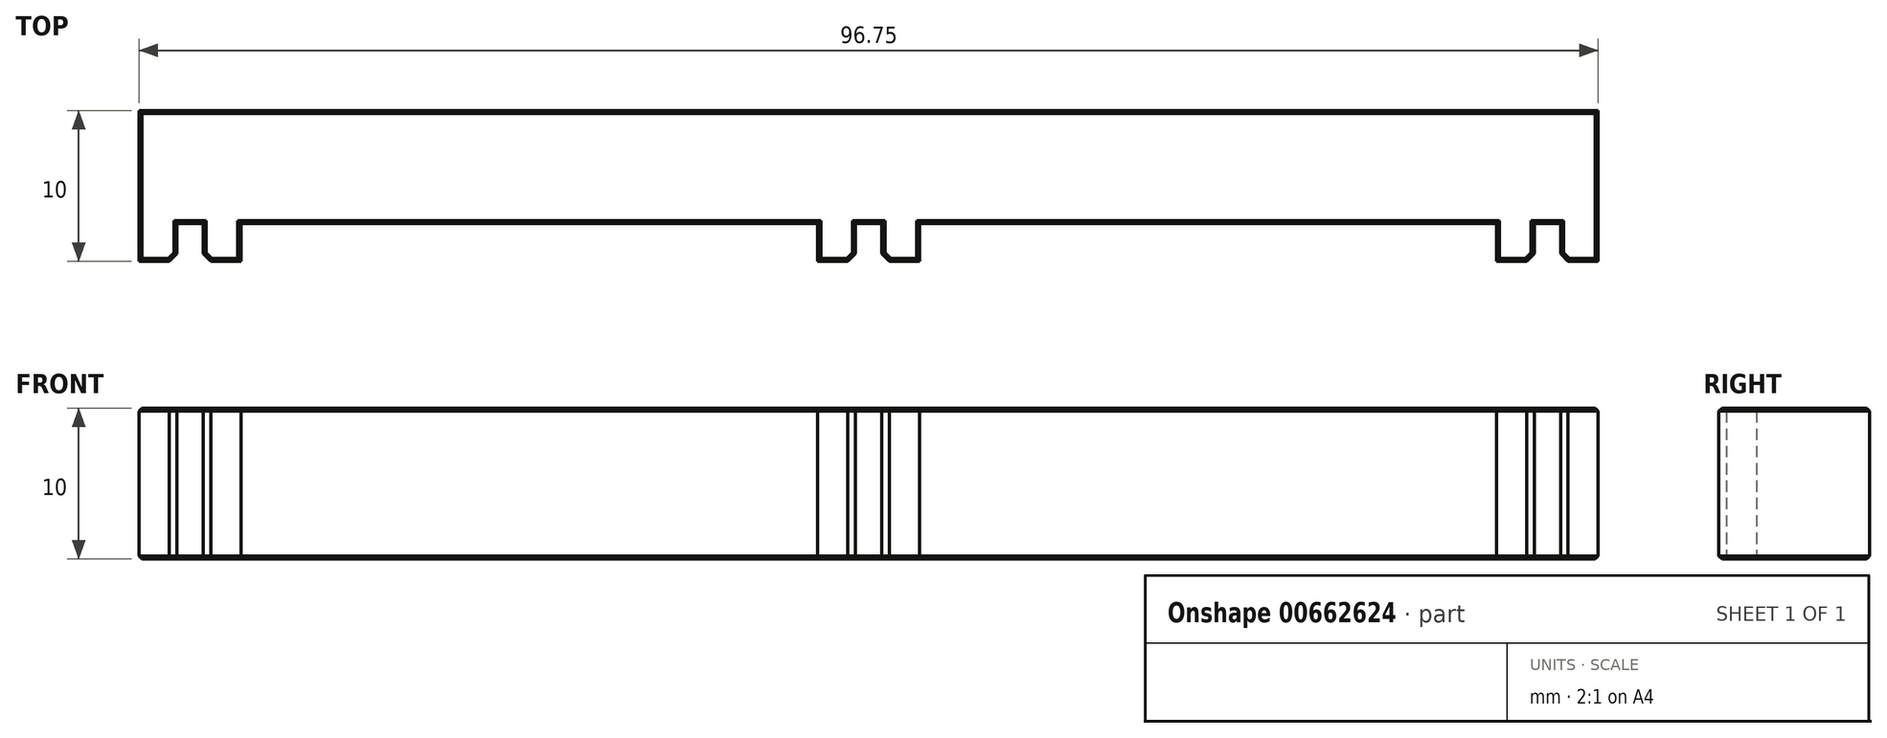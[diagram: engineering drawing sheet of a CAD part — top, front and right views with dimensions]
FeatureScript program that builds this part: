
annotation { "Feature Type Name" : "Feature", "Feature Type Description" : "" }
export const myFeature = defineFeature(function(context is Context, id is Id, definition is map)
    precondition{}
    {
        {
            var Q0;
            Q0=qCreatedBy(makeId("Top.planeOp"),FACE);
            var sketch = newSketch(context, id + "F0", { "sketchPlane" : qUnion([Q0])});
            skLineSegment(sketch, "E0", {"start": v(-51.46, 0) * mm, "end": v(-51.46, 10) * mm});
            skLineSegment(sketch, "E1", {"start": v(-51.46, 10) * mm, "end": v(45.3, 10) * mm});
            skLineSegment(sketch, "E2", {"start": v(45.3, 10) * mm, "end": v(45.3, 0) * mm});
            skLineSegment(sketch, "E3", {"start": v(45.3, 0) * mm, "end": v(42.8, 0) * mm});
            skLineSegment(sketch, "E4", {"start": v(42.8, 0) * mm, "end": v(42.8, 2.5) * mm});
            skLineSegment(sketch, "E5", {"start": v(42.8, 2.5) * mm, "end": v(41.04, 2.5) * mm});
            skLineSegment(sketch, "E6", {"start": v(41.04, 2.5) * mm, "end": v(41.04, 0) * mm});
            skLineSegment(sketch, "E7", {"start": v(41.04, 0) * mm, "end": v(38.54, 0) * mm});
            skLineSegment(sketch, "E8", {"start": v(38.54, 2.5) * mm, "end": v(38.54, 0) * mm});
            skLineSegment(sketch, "E9", {"start": v(38.54, 2.5) * mm, "end": v(0.3, 2.5) * mm});
            skLineSegment(sketch, "E10", {"start": v(0.3, 2.5) * mm, "end": v(0.3, 0) * mm});
            skLineSegment(sketch, "E11", {"start": v(0.3, 0) * mm, "end": v(-2.2, 0) * mm});
            skLineSegment(sketch, "E12", {"start": v(-2.2, 2.5) * mm, "end": v(-2.2, 0) * mm});
            skLineSegment(sketch, "E13", {"start": v(-2.2, 2.5) * mm, "end": v(-3.96, 2.5) * mm});
            skLineSegment(sketch, "E14", {"start": v(-3.96, 2.5) * mm, "end": v(-3.96, 0) * mm});
            skLineSegment(sketch, "E15", {"start": v(-3.96, 0) * mm, "end": v(-6.46, 0) * mm});
            skLineSegment(sketch, "E16", {"start": v(-6.46, 2.5) * mm, "end": v(-6.46, 0) * mm});
            skLineSegment(sketch, "E17", {"start": v(-6.46, 2.5) * mm, "end": v(-44.7, 2.5) * mm});
            skLineSegment(sketch, "E18", {"start": v(-44.7, 2.5) * mm, "end": v(-44.7, 0) * mm});
            skLineSegment(sketch, "E19", {"start": v(-44.7, 0) * mm, "end": v(-47.2, 0) * mm});
            skLineSegment(sketch, "E20", {"start": v(-47.2, 0) * mm, "end": v(-47.2, 2.5) * mm});
            skLineSegment(sketch, "E21", {"start": v(-47.2, 2.5) * mm, "end": v(-48.96, 2.5) * mm});
            skLineSegment(sketch, "E22", {"start": v(-48.96, 2.5) * mm, "end": v(-48.96, 0) * mm});
            skLineSegment(sketch, "E23", {"start": v(-48.96, 0) * mm, "end": v(-51.46, 0) * mm});
            skSolve(sketch);
        }
        {
            var Q0;
            Q0=makeQuery(id+"F0.imprint","IMPRINT",FACE,{"disambiguationData":[TD([[makeQuery(id+"F0.imprint","IMPRINT",EDGE,{"derivedFrom":sQuery(id+"F0.wireOp",EDGE,"E0")}),-1.0]])]});
            extrude(context, id + "F1", {"entities" : qUnion([Q0]), "depth" : 10 * mm, "offsetDistance" : 25 * mm});
        }
        {
            var Q0;
            Q0=makeQuery(id+"F1.opExtrude","SWEPT_EDGE",EDGE,{"disambiguationData":[OSD([sQuery(id+"F0.wireOp",EDGE,"E22"),sQuery(id+"F0.wireOp",EDGE,"E23")])]});
            var Q1;
            Q1=makeQuery(id+"F1.opExtrude","SWEPT_EDGE",EDGE,{"disambiguationData":[OSD([sQuery(id+"F0.wireOp",EDGE,"E19"),sQuery(id+"F0.wireOp",EDGE,"E20")])]});
            var Q2;
            Q2=makeQuery(id+"F1.opExtrude","SWEPT_EDGE",EDGE,{"disambiguationData":[OSD([sQuery(id+"F0.wireOp",EDGE,"E11"),sQuery(id+"F0.wireOp",EDGE,"E12")])]});
            var Q3;
            Q3=makeQuery(id+"F1.opExtrude","SWEPT_EDGE",EDGE,{"disambiguationData":[OSD([sQuery(id+"F0.wireOp",EDGE,"E14"),sQuery(id+"F0.wireOp",EDGE,"E15")])]});
            var Q4;
            Q4=makeQuery(id+"F1.opExtrude","SWEPT_EDGE",EDGE,{"disambiguationData":[OSD([sQuery(id+"F0.wireOp",EDGE,"E3"),sQuery(id+"F0.wireOp",EDGE,"E4")])]});
            var Q5;
            Q5=makeQuery(id+"F1.opExtrude","SWEPT_EDGE",EDGE,{"disambiguationData":[OSD([sQuery(id+"F0.wireOp",EDGE,"E6"),sQuery(id+"F0.wireOp",EDGE,"E7")])]});
            chamfer(context, id + "F2", {"entities" : qUnion([Q0, Q1, Q2, Q3, Q4, Q5]), "width" : .5 * mm, "tangentPropagation" : true});
        }
        {
            var Q0;
            Q0=makeQuery(id+"F1.opExtrude","CAP_FACE",FACE,{"disambiguationData":[OSD([sQuery(id+"F0.wireOp",EDGE,"E0"),sQuery(id+"F0.wireOp",EDGE,"E1"),sQuery(id+"F0.wireOp",EDGE,"E2"),sQuery(id+"F0.wireOp",EDGE,"E3"),sQuery(id+"F0.wireOp",EDGE,"E4"),sQuery(id+"F0.wireOp",EDGE,"E5"),sQuery(id+"F0.wireOp",EDGE,"E6"),sQuery(id+"F0.wireOp",EDGE,"E7"),sQuery(id+"F0.wireOp",EDGE,"E8"),sQuery(id+"F0.wireOp",EDGE,"E9"),sQuery(id+"F0.wireOp",EDGE,"E10"),sQuery(id+"F0.wireOp",EDGE,"E11"),sQuery(id+"F0.wireOp",EDGE,"E12"),sQuery(id+"F0.wireOp",EDGE,"E13"),sQuery(id+"F0.wireOp",EDGE,"E14"),sQuery(id+"F0.wireOp",EDGE,"E15"),sQuery(id+"F0.wireOp",EDGE,"E16"),sQuery(id+"F0.wireOp",EDGE,"E17"),sQuery(id+"F0.wireOp",EDGE,"E18"),sQuery(id+"F0.wireOp",EDGE,"E19"),sQuery(id+"F0.wireOp",EDGE,"E20"),sQuery(id+"F0.wireOp",EDGE,"E21"),sQuery(id+"F0.wireOp",EDGE,"E22"),sQuery(id+"F0.wireOp",EDGE,"E23")])],"isStart":false});
            var Q1;
            Q1=makeQuery(id+"F1.opExtrude","CAP_FACE",FACE,{"disambiguationData":[OSD([sQuery(id+"F0.wireOp",EDGE,"E0"),sQuery(id+"F0.wireOp",EDGE,"E1"),sQuery(id+"F0.wireOp",EDGE,"E2"),sQuery(id+"F0.wireOp",EDGE,"E3"),sQuery(id+"F0.wireOp",EDGE,"E4"),sQuery(id+"F0.wireOp",EDGE,"E5"),sQuery(id+"F0.wireOp",EDGE,"E6"),sQuery(id+"F0.wireOp",EDGE,"E7"),sQuery(id+"F0.wireOp",EDGE,"E8"),sQuery(id+"F0.wireOp",EDGE,"E9"),sQuery(id+"F0.wireOp",EDGE,"E10"),sQuery(id+"F0.wireOp",EDGE,"E11"),sQuery(id+"F0.wireOp",EDGE,"E12"),sQuery(id+"F0.wireOp",EDGE,"E13"),sQuery(id+"F0.wireOp",EDGE,"E14"),sQuery(id+"F0.wireOp",EDGE,"E15"),sQuery(id+"F0.wireOp",EDGE,"E16"),sQuery(id+"F0.wireOp",EDGE,"E17"),sQuery(id+"F0.wireOp",EDGE,"E18"),sQuery(id+"F0.wireOp",EDGE,"E19"),sQuery(id+"F0.wireOp",EDGE,"E20"),sQuery(id+"F0.wireOp",EDGE,"E21"),sQuery(id+"F0.wireOp",EDGE,"E22"),sQuery(id+"F0.wireOp",EDGE,"E23")])],"isStart":true});
            chamfer(context, id + "F3", {"entities" : qUnion([Q0, Q1]), "width" : .2 * mm, "tangentPropagation" : true});
        }
    });
